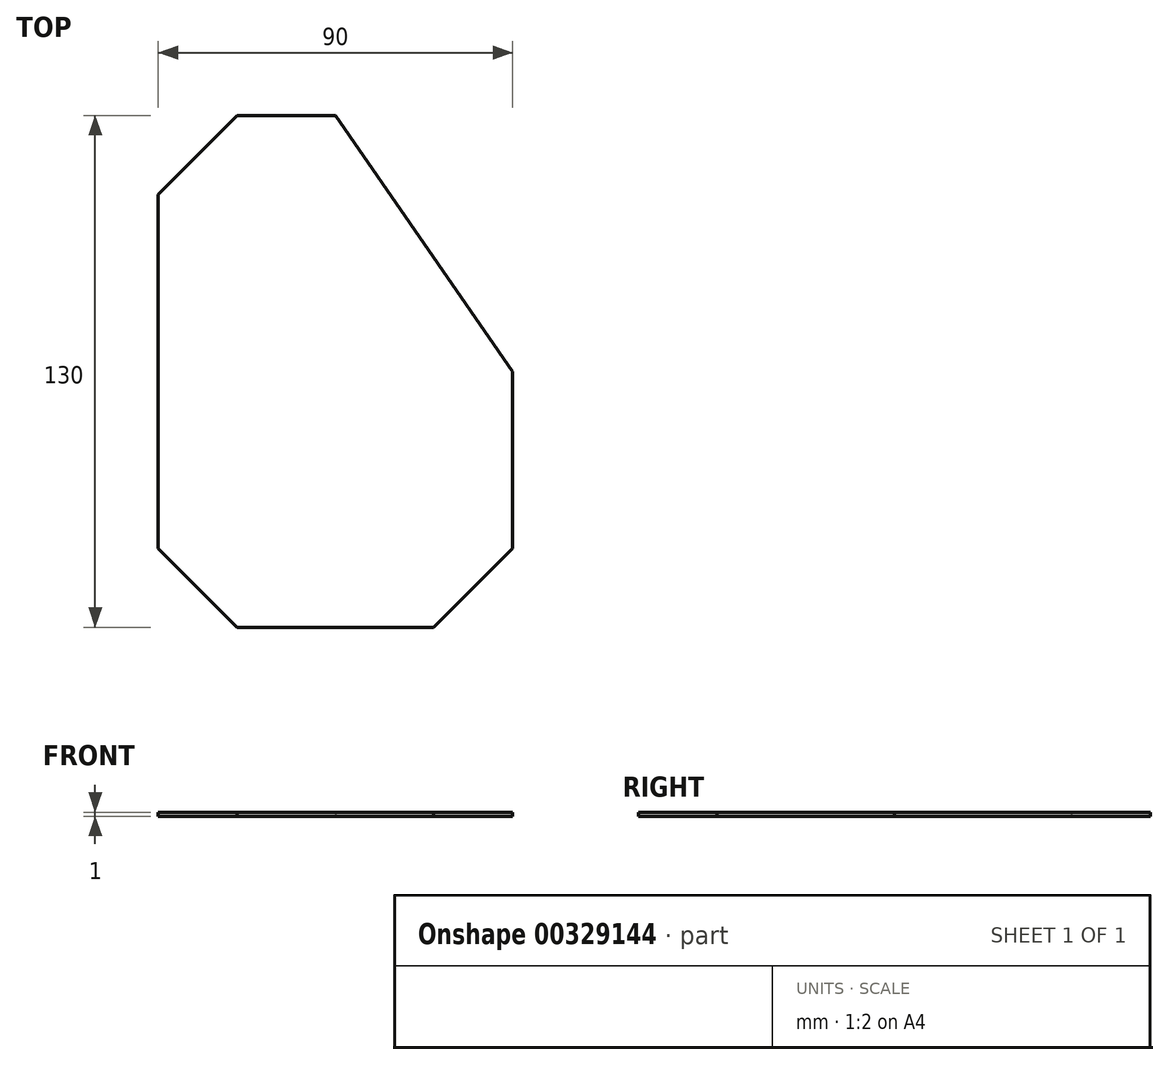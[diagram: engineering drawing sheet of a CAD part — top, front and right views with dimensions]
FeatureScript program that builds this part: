
annotation { "Feature Type Name" : "Feature", "Feature Type Description" : "" }
export const myFeature = defineFeature(function(context is Context, id is Id, definition is map)
    precondition{}
    {
        {
            var Q0;
            Q0=qCreatedBy(makeId("Top.planeOp"),FACE);
            var sketch = newSketch(context, id + "F0", { "sketchPlane" : qUnion([Q0])});
            skLineSegment(sketch, "E0", {"start": v(-38.2, 69.38) * mm, "end": v(-38.2, -60.62) * mm});
            skLineSegment(sketch, "E1", {"start": v(-38.2, -60.62) * mm, "end": v(51.8, -60.62) * mm});
            skLineSegment(sketch, "E2", {"start": v(51.8, -60.62) * mm, "end": v(51.8, 4.38) * mm});
            skLineSegment(sketch, "E3", {"start": v(51.8, 4.38) * mm, "end": v(6.8, 69.38) * mm});
            skLineSegment(sketch, "E4", {"start": v(6.8, 69.38) * mm, "end": v(-38.2, 69.38) * mm});
            skSolve(sketch);
        }
        {
            var Q0;
            Q0 = qSketchRegion(id + "F0", true);
            extrude(context, id + "F1", {"entities" : qUnion([Q0]), "depth" : 1 * mm});
        }
        {
            var Q0;
            Q0=makeQuery(id+"F1.opExtrude","SWEPT_EDGE",EDGE,{"disambiguationData":[OSD([sQuery(id+"F0.wireOp",EDGE,"E1"),sQuery(id+"F0.wireOp",EDGE,"E2")])]});
            chamfer(context, id + "F2", {"entities" : qUnion([Q0]), "width" : 20 * mm, "tangentPropagation" : true});
        }
        {
            var Q0;
            Q0=makeQuery(id+"F1.opExtrude","SWEPT_EDGE",EDGE,{"disambiguationData":[OSD([sQuery(id+"F0.wireOp",EDGE,"E0"),sQuery(id+"F0.wireOp",EDGE,"E1")])]});
            chamfer(context, id + "F3", {"entities" : qUnion([Q0]), "width" : 20 * mm, "tangentPropagation" : true});
        }
        {
            var Q0;
            Q0=makeQuery(id+"F1.opExtrude","SWEPT_EDGE",EDGE,{"disambiguationData":[OSD([sQuery(id+"F0.wireOp",EDGE,"E0"),sQuery(id+"F0.wireOp",EDGE,"E4")])]});
            chamfer(context, id + "F4", {"entities" : qUnion([Q0]), "width" : 20 * mm, "tangentPropagation" : true});
        }
    });
